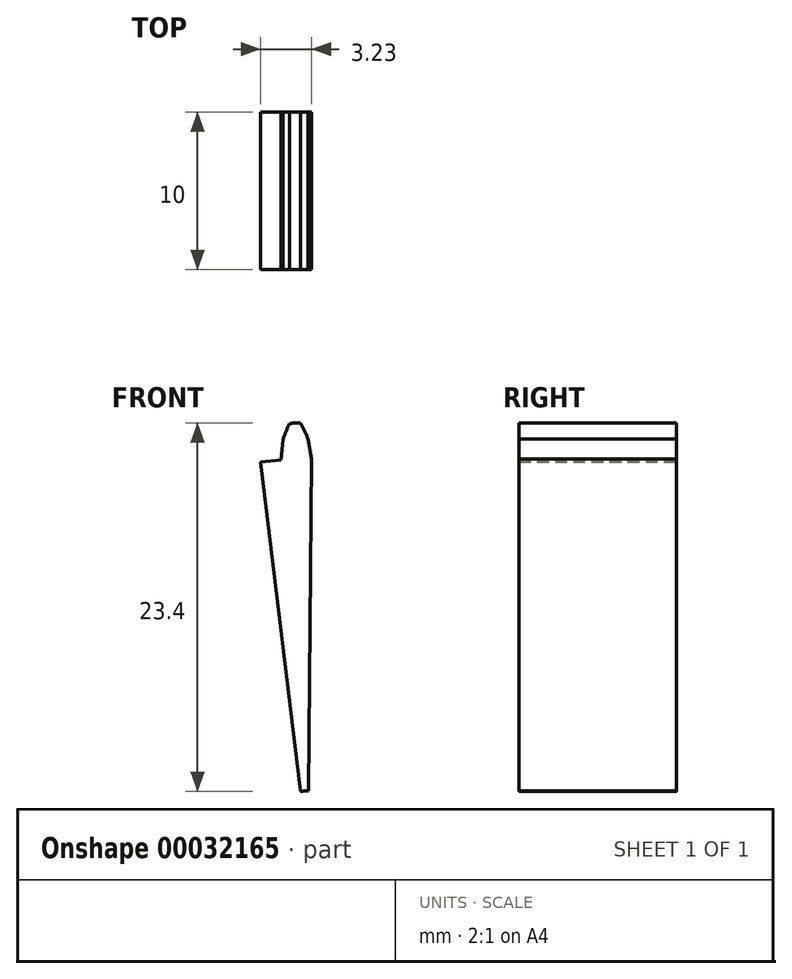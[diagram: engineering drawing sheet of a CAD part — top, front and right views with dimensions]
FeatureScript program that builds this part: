
annotation { "Feature Type Name" : "Feature", "Feature Type Description" : "" }
export const myFeature = defineFeature(function(context is Context, id is Id, definition is map)
    precondition{}
    {
        {
            var Q0;
            Q0=qCreatedBy(makeId("Front.planeOp"),FACE);
            var sketch = newSketch(context, id + "F0", { "sketchPlane" : qUnion([Q0])});
            skArc(sketch, "E0.trimOffspring", {"start": v(0, 26.31) * mm, "mid": v(-0.22, 26.83) * mm, "end": v(-0.48, 27.32) * mm});
            skArc(sketch, "E1.0.MirrorCS", {"start": v(-1.59, 26.26) * mm, "mid": v(-1.4, 26.8) * mm, "end": v(-1.17, 27.3) * mm});
            skArc(sketch, "E2.trimOffspring", {"start": v(-0.48, 27.32) * mm, "mid": v(-0.83, 27.31) * mm, "end": v(-1.17, 27.3) * mm});
            skCircle(sketch, "E3", {"center": v(0, -0.03) * mm, "radius": 29 * mm});
            skArc(sketch, "E4.trimOffspring", {"start": v(1.48, 24.98) * mm, "mid": v(0.85, 25.02) * mm, "end": v(0.21, 25.04) * mm});
            skLineSegment(sketch, "E5", {"start": v(-3.02, 24.86) * mm, "end": v(-1.72, 24.98) * mm});
            skCircle(sketch, "E6", {"center": v(0, 0) * mm, "radius": 3.95 * mm});
            skLineSegment(sketch, "E7", {"start": v(-3.5, 28.76) * mm, "end": v(0, 0) * mm});
            skLineSegment(sketch, "E8", {"start": v(-1.59, 26.26) * mm, "end": v(-1.72, 24.98) * mm});
            skLineSegment(sketch, "E9", {"start": v(0, 26.31) * mm, "end": v(0.21, 25.04) * mm});
            skLineSegment(sketch, "E10", {"start": v(0.24, 28.97) * mm, "end": v(0, 0) * mm});
            skSolve(sketch);
        }
        {
            var Q0;
            Q0=makeQuery(id+"FG2zr5kD53DtZhP_0.opExtrude","CAP_FACE",FACE,{"disambiguationData":[OSD([sQuery(id+"F0.wireOp",EDGE,"38f0ead0-3dfe-4054-9ca8-f6ac89a4f2fc"),sQuery(id+"F0.wireOp",EDGE,"E0.trimOffspring"),sQuery(id+"F0.wireOp",EDGE,"E1.0.MirrorCS"),sQuery(id+"F0.wireOp",EDGE,"ad14948e-b5b9-4d29-acd9-736fc249e560.0.MirrorCS"),sQuery(id+"F0.wireOp",EDGE,"E2.trimOffspring"),sQuery(id+"F0.wireOp",EDGE,"63f2db29-570f-450b-bac2-a88f50f61318.1.0"),sQuery(id+"F0.wireOp",EDGE,"63f2db29-570f-450b-bac2-a88f50f61318.1.1"),sQuery(id+"F0.wireOp",EDGE,"63f2db29-570f-450b-bac2-a88f50f61318.1.2"),sQuery(id+"F0.wireOp",EDGE,"63f2db29-570f-450b-bac2-a88f50f61318.1.3"),sQuery(id+"F0.wireOp",EDGE,"63f2db29-570f-450b-bac2-a88f50f61318.1.4"),sQuery(id+"F0.wireOp",EDGE,"63f2db29-570f-450b-bac2-a88f50f61318.2.0"),sQuery(id+"F0.wireOp",EDGE,"63f2db29-570f-450b-bac2-a88f50f61318.2.1"),sQuery(id+"F0.wireOp",EDGE,"63f2db29-570f-450b-bac2-a88f50f61318.2.2"),sQuery(id+"F0.wireOp",EDGE,"63f2db29-570f-450b-bac2-a88f50f61318.2.3"),sQuery(id+"F0.wireOp",EDGE,"63f2db29-570f-450b-bac2-a88f50f61318.2.4"),sQuery(id+"F0.wireOp",EDGE,"63f2db29-570f-450b-bac2-a88f50f61318.3.0"),sQuery(id+"F0.wireOp",EDGE,"63f2db29-570f-450b-bac2-a88f50f61318.3.1"),sQuery(id+"F0.wireOp",EDGE,"63f2db29-570f-450b-bac2-a88f50f61318.3.2"),sQuery(id+"F0.wireOp",EDGE,"63f2db29-570f-450b-bac2-a88f50f61318.3.3"),sQuery(id+"F0.wireOp",EDGE,"63f2db29-570f-450b-bac2-a88f50f61318.3.4"),sQuery(id+"F0.wireOp",EDGE,"63f2db29-570f-450b-bac2-a88f50f61318.4.0"),sQuery(id+"F0.wireOp",EDGE,"63f2db29-570f-450b-bac2-a88f50f61318.4.1"),sQuery(id+"F0.wireOp",EDGE,"63f2db29-570f-450b-bac2-a88f50f61318.4.2"),sQuery(id+"F0.wireOp",EDGE,"63f2db29-570f-450b-bac2-a88f50f61318.4.3"),sQuery(id+"F0.wireOp",EDGE,"63f2db29-570f-450b-bac2-a88f50f61318.4.4"),sQuery(id+"F0.wireOp",EDGE,"63f2db29-570f-450b-bac2-a88f50f61318.5.0"),sQuery(id+"F0.wireOp",EDGE,"63f2db29-570f-450b-bac2-a88f50f61318.5.1"),sQuery(id+"F0.wireOp",EDGE,"63f2db29-570f-450b-bac2-a88f50f61318.5.2"),sQuery(id+"F0.wireOp",EDGE,"63f2db29-570f-450b-bac2-a88f50f61318.5.3"),sQuery(id+"F0.wireOp",EDGE,"63f2db29-570f-450b-bac2-a88f50f61318.5.4"),sQuery(id+"F0.wireOp",EDGE,"63f2db29-570f-450b-bac2-a88f50f61318.6.0"),sQuery(id+"F0.wireOp",EDGE,"63f2db29-570f-450b-bac2-a88f50f61318.6.1"),sQuery(id+"F0.wireOp",EDGE,"63f2db29-570f-450b-bac2-a88f50f61318.6.2"),sQuery(id+"F0.wireOp",EDGE,"63f2db29-570f-450b-bac2-a88f50f61318.6.3"),sQuery(id+"F0.wireOp",EDGE,"63f2db29-570f-450b-bac2-a88f50f61318.6.4"),sQuery(id+"F0.wireOp",EDGE,"63f2db29-570f-450b-bac2-a88f50f61318.7.0"),sQuery(id+"F0.wireOp",EDGE,"63f2db29-570f-450b-bac2-a88f50f61318.7.1"),sQuery(id+"F0.wireOp",EDGE,"63f2db29-570f-450b-bac2-a88f50f61318.7.2"),sQuery(id+"F0.wireOp",EDGE,"63f2db29-570f-450b-bac2-a88f50f61318.7.3"),sQuery(id+"F0.wireOp",EDGE,"63f2db29-570f-450b-bac2-a88f50f61318.7.4"),sQuery(id+"F0.wireOp",EDGE,"63f2db29-570f-450b-bac2-a88f50f61318.8.0"),sQuery(id+"F0.wireOp",EDGE,"63f2db29-570f-450b-bac2-a88f50f61318.8.1"),sQuery(id+"F0.wireOp",EDGE,"63f2db29-570f-450b-bac2-a88f50f61318.8.2"),sQuery(id+"F0.wireOp",EDGE,"63f2db29-570f-450b-bac2-a88f50f61318.8.3"),sQuery(id+"F0.wireOp",EDGE,"63f2db29-570f-450b-bac2-a88f50f61318.8.4"),sQuery(id+"F0.wireOp",EDGE,"63f2db29-570f-450b-bac2-a88f50f61318.9.0"),sQuery(id+"F0.wireOp",EDGE,"63f2db29-570f-450b-bac2-a88f50f61318.9.1"),sQuery(id+"F0.wireOp",EDGE,"63f2db29-570f-450b-bac2-a88f50f61318.9.2"),sQuery(id+"F0.wireOp",EDGE,"63f2db29-570f-450b-bac2-a88f50f61318.9.3"),sQuery(id+"F0.wireOp",EDGE,"63f2db29-570f-450b-bac2-a88f50f61318.9.4"),sQuery(id+"F0.wireOp",EDGE,"63f2db29-570f-450b-bac2-a88f50f61318.10.0"),sQuery(id+"F0.wireOp",EDGE,"63f2db29-570f-450b-bac2-a88f50f61318.10.1"),sQuery(id+"F0.wireOp",EDGE,"63f2db29-570f-450b-bac2-a88f50f61318.10.2"),sQuery(id+"F0.wireOp",EDGE,"63f2db29-570f-450b-bac2-a88f50f61318.10.3"),sQuery(id+"F0.wireOp",EDGE,"63f2db29-570f-450b-bac2-a88f50f61318.10.4"),sQuery(id+"F0.wireOp",EDGE,"63f2db29-570f-450b-bac2-a88f50f61318.11.0"),sQuery(id+"F0.wireOp",EDGE,"63f2db29-570f-450b-bac2-a88f50f61318.11.1"),sQuery(id+"F0.wireOp",EDGE,"63f2db29-570f-450b-bac2-a88f50f61318.11.2"),sQuery(id+"F0.wireOp",EDGE,"63f2db29-570f-450b-bac2-a88f50f61318.11.3"),sQuery(id+"F0.wireOp",EDGE,"63f2db29-570f-450b-bac2-a88f50f61318.11.4"),sQuery(id+"F0.wireOp",EDGE,"63f2db29-570f-450b-bac2-a88f50f61318.12.0"),sQuery(id+"F0.wireOp",EDGE,"63f2db29-570f-450b-bac2-a88f50f61318.12.1"),sQuery(id+"F0.wireOp",EDGE,"63f2db29-570f-450b-bac2-a88f50f61318.12.2"),sQuery(id+"F0.wireOp",EDGE,"63f2db29-570f-450b-bac2-a88f50f61318.12.3"),sQuery(id+"F0.wireOp",EDGE,"63f2db29-570f-450b-bac2-a88f50f61318.12.4"),sQuery(id+"F0.wireOp",EDGE,"63f2db29-570f-450b-bac2-a88f50f61318.13.0"),sQuery(id+"F0.wireOp",EDGE,"63f2db29-570f-450b-bac2-a88f50f61318.13.1"),sQuery(id+"F0.wireOp",EDGE,"63f2db29-570f-450b-bac2-a88f50f61318.13.2"),sQuery(id+"F0.wireOp",EDGE,"63f2db29-570f-450b-bac2-a88f50f61318.13.3"),sQuery(id+"F0.wireOp",EDGE,"63f2db29-570f-450b-bac2-a88f50f61318.13.4"),sQuery(id+"F0.wireOp",EDGE,"63f2db29-570f-450b-bac2-a88f50f61318.14.0"),sQuery(id+"F0.wireOp",EDGE,"63f2db29-570f-450b-bac2-a88f50f61318.14.1"),sQuery(id+"F0.wireOp",EDGE,"63f2db29-570f-450b-bac2-a88f50f61318.14.2"),sQuery(id+"F0.wireOp",EDGE,"63f2db29-570f-450b-bac2-a88f50f61318.14.3"),sQuery(id+"F0.wireOp",EDGE,"63f2db29-570f-450b-bac2-a88f50f61318.14.4"),sQuery(id+"F0.wireOp",EDGE,"63f2db29-570f-450b-bac2-a88f50f61318.15.0"),sQuery(id+"F0.wireOp",EDGE,"63f2db29-570f-450b-bac2-a88f50f61318.15.1"),sQuery(id+"F0.wireOp",EDGE,"63f2db29-570f-450b-bac2-a88f50f61318.15.2"),sQuery(id+"F0.wireOp",EDGE,"63f2db29-570f-450b-bac2-a88f50f61318.15.3"),sQuery(id+"F0.wireOp",EDGE,"63f2db29-570f-450b-bac2-a88f50f61318.15.4"),sQuery(id+"F0.wireOp",EDGE,"63f2db29-570f-450b-bac2-a88f50f61318.16.0"),sQuery(id+"F0.wireOp",EDGE,"63f2db29-570f-450b-bac2-a88f50f61318.16.1"),sQuery(id+"F0.wireOp",EDGE,"63f2db29-570f-450b-bac2-a88f50f61318.16.2"),sQuery(id+"F0.wireOp",EDGE,"63f2db29-570f-450b-bac2-a88f50f61318.16.3"),sQuery(id+"F0.wireOp",EDGE,"63f2db29-570f-450b-bac2-a88f50f61318.16.4"),sQuery(id+"F0.wireOp",EDGE,"63f2db29-570f-450b-bac2-a88f50f61318.17.0"),sQuery(id+"F0.wireOp",EDGE,"63f2db29-570f-450b-bac2-a88f50f61318.17.1"),sQuery(id+"F0.wireOp",EDGE,"63f2db29-570f-450b-bac2-a88f50f61318.17.2"),sQuery(id+"F0.wireOp",EDGE,"63f2db29-570f-450b-bac2-a88f50f61318.17.3"),sQuery(id+"F0.wireOp",EDGE,"63f2db29-570f-450b-bac2-a88f50f61318.17.4"),sQuery(id+"F0.wireOp",EDGE,"63f2db29-570f-450b-bac2-a88f50f61318.18.0"),sQuery(id+"F0.wireOp",EDGE,"63f2db29-570f-450b-bac2-a88f50f61318.18.1"),sQuery(id+"F0.wireOp",EDGE,"63f2db29-570f-450b-bac2-a88f50f61318.18.2"),sQuery(id+"F0.wireOp",EDGE,"63f2db29-570f-450b-bac2-a88f50f61318.18.3"),sQuery(id+"F0.wireOp",EDGE,"63f2db29-570f-450b-bac2-a88f50f61318.18.4"),sQuery(id+"F0.wireOp",EDGE,"63f2db29-570f-450b-bac2-a88f50f61318.19.0"),sQuery(id+"F0.wireOp",EDGE,"63f2db29-570f-450b-bac2-a88f50f61318.19.1"),sQuery(id+"F0.wireOp",EDGE,"63f2db29-570f-450b-bac2-a88f50f61318.19.2"),sQuery(id+"F0.wireOp",EDGE,"63f2db29-570f-450b-bac2-a88f50f61318.19.3"),sQuery(id+"F0.wireOp",EDGE,"63f2db29-570f-450b-bac2-a88f50f61318.19.4"),sQuery(id+"F0.wireOp",EDGE,"63f2db29-570f-450b-bac2-a88f50f61318.20.0"),sQuery(id+"F0.wireOp",EDGE,"63f2db29-570f-450b-bac2-a88f50f61318.20.1"),sQuery(id+"F0.wireOp",EDGE,"63f2db29-570f-450b-bac2-a88f50f61318.20.2"),sQuery(id+"F0.wireOp",EDGE,"63f2db29-570f-450b-bac2-a88f50f61318.20.3"),sQuery(id+"F0.wireOp",EDGE,"63f2db29-570f-450b-bac2-a88f50f61318.20.4"),sQuery(id+"F0.wireOp",EDGE,"63f2db29-570f-450b-bac2-a88f50f61318.21.0"),sQuery(id+"F0.wireOp",EDGE,"63f2db29-570f-450b-bac2-a88f50f61318.21.1"),sQuery(id+"F0.wireOp",EDGE,"63f2db29-570f-450b-bac2-a88f50f61318.21.2"),sQuery(id+"F0.wireOp",EDGE,"63f2db29-570f-450b-bac2-a88f50f61318.21.3"),sQuery(id+"F0.wireOp",EDGE,"63f2db29-570f-450b-bac2-a88f50f61318.21.4"),sQuery(id+"F0.wireOp",EDGE,"63f2db29-570f-450b-bac2-a88f50f61318.22.0"),sQuery(id+"F0.wireOp",EDGE,"63f2db29-570f-450b-bac2-a88f50f61318.22.1"),sQuery(id+"F0.wireOp",EDGE,"63f2db29-570f-450b-bac2-a88f50f61318.22.2"),sQuery(id+"F0.wireOp",EDGE,"63f2db29-570f-450b-bac2-a88f50f61318.22.3"),sQuery(id+"F0.wireOp",EDGE,"63f2db29-570f-450b-bac2-a88f50f61318.22.4"),sQuery(id+"F0.wireOp",EDGE,"63f2db29-570f-450b-bac2-a88f50f61318.23.0"),sQuery(id+"F0.wireOp",EDGE,"63f2db29-570f-450b-bac2-a88f50f61318.23.1"),sQuery(id+"F0.wireOp",EDGE,"63f2db29-570f-450b-bac2-a88f50f61318.23.2"),sQuery(id+"F0.wireOp",EDGE,"63f2db29-570f-450b-bac2-a88f50f61318.23.3"),sQuery(id+"F0.wireOp",EDGE,"63f2db29-570f-450b-bac2-a88f50f61318.23.4"),sQuery(id+"F0.wireOp",EDGE,"63f2db29-570f-450b-bac2-a88f50f61318.24.0"),sQuery(id+"F0.wireOp",EDGE,"63f2db29-570f-450b-bac2-a88f50f61318.24.1"),sQuery(id+"F0.wireOp",EDGE,"63f2db29-570f-450b-bac2-a88f50f61318.24.2"),sQuery(id+"F0.wireOp",EDGE,"63f2db29-570f-450b-bac2-a88f50f61318.24.3"),sQuery(id+"F0.wireOp",EDGE,"63f2db29-570f-450b-bac2-a88f50f61318.24.4"),sQuery(id+"F0.wireOp",EDGE,"63f2db29-570f-450b-bac2-a88f50f61318.25.0"),sQuery(id+"F0.wireOp",EDGE,"63f2db29-570f-450b-bac2-a88f50f61318.25.1"),sQuery(id+"F0.wireOp",EDGE,"63f2db29-570f-450b-bac2-a88f50f61318.25.2"),sQuery(id+"F0.wireOp",EDGE,"63f2db29-570f-450b-bac2-a88f50f61318.25.3"),sQuery(id+"F0.wireOp",EDGE,"63f2db29-570f-450b-bac2-a88f50f61318.25.4"),sQuery(id+"F0.wireOp",EDGE,"63f2db29-570f-450b-bac2-a88f50f61318.26.0"),sQuery(id+"F0.wireOp",EDGE,"63f2db29-570f-450b-bac2-a88f50f61318.26.1"),sQuery(id+"F0.wireOp",EDGE,"63f2db29-570f-450b-bac2-a88f50f61318.26.2"),sQuery(id+"F0.wireOp",EDGE,"63f2db29-570f-450b-bac2-a88f50f61318.26.3"),sQuery(id+"F0.wireOp",EDGE,"63f2db29-570f-450b-bac2-a88f50f61318.26.4"),sQuery(id+"F0.wireOp",EDGE,"63f2db29-570f-450b-bac2-a88f50f61318.27.0"),sQuery(id+"F0.wireOp",EDGE,"63f2db29-570f-450b-bac2-a88f50f61318.27.1"),sQuery(id+"F0.wireOp",EDGE,"63f2db29-570f-450b-bac2-a88f50f61318.27.2"),sQuery(id+"F0.wireOp",EDGE,"63f2db29-570f-450b-bac2-a88f50f61318.27.3"),sQuery(id+"F0.wireOp",EDGE,"63f2db29-570f-450b-bac2-a88f50f61318.27.4"),sQuery(id+"F0.wireOp",EDGE,"63f2db29-570f-450b-bac2-a88f50f61318.28.0"),sQuery(id+"F0.wireOp",EDGE,"63f2db29-570f-450b-bac2-a88f50f61318.28.1"),sQuery(id+"F0.wireOp",EDGE,"63f2db29-570f-450b-bac2-a88f50f61318.28.2"),sQuery(id+"F0.wireOp",EDGE,"63f2db29-570f-450b-bac2-a88f50f61318.28.3"),sQuery(id+"F0.wireOp",EDGE,"63f2db29-570f-450b-bac2-a88f50f61318.28.4"),sQuery(id+"F0.wireOp",EDGE,"63f2db29-570f-450b-bac2-a88f50f61318.29.0"),sQuery(id+"F0.wireOp",EDGE,"63f2db29-570f-450b-bac2-a88f50f61318.29.1"),sQuery(id+"F0.wireOp",EDGE,"63f2db29-570f-450b-bac2-a88f50f61318.29.2"),sQuery(id+"F0.wireOp",EDGE,"63f2db29-570f-450b-bac2-a88f50f61318.29.3"),sQuery(id+"F0.wireOp",EDGE,"63f2db29-570f-450b-bac2-a88f50f61318.29.4"),sQuery(id+"F0.wireOp",EDGE,"63f2db29-570f-450b-bac2-a88f50f61318.30.0"),sQuery(id+"F0.wireOp",EDGE,"63f2db29-570f-450b-bac2-a88f50f61318.30.1"),sQuery(id+"F0.wireOp",EDGE,"63f2db29-570f-450b-bac2-a88f50f61318.30.2"),sQuery(id+"F0.wireOp",EDGE,"63f2db29-570f-450b-bac2-a88f50f61318.30.3"),sQuery(id+"F0.wireOp",EDGE,"63f2db29-570f-450b-bac2-a88f50f61318.30.4"),sQuery(id+"F0.wireOp",EDGE,"63f2db29-570f-450b-bac2-a88f50f61318.31.0"),sQuery(id+"F0.wireOp",EDGE,"63f2db29-570f-450b-bac2-a88f50f61318.31.1"),sQuery(id+"F0.wireOp",EDGE,"63f2db29-570f-450b-bac2-a88f50f61318.31.2"),sQuery(id+"F0.wireOp",EDGE,"63f2db29-570f-450b-bac2-a88f50f61318.31.3"),sQuery(id+"F0.wireOp",EDGE,"63f2db29-570f-450b-bac2-a88f50f61318.31.4"),sQuery(id+"F0.wireOp",EDGE,"63f2db29-570f-450b-bac2-a88f50f61318.32.0"),sQuery(id+"F0.wireOp",EDGE,"63f2db29-570f-450b-bac2-a88f50f61318.32.1"),sQuery(id+"F0.wireOp",EDGE,"63f2db29-570f-450b-bac2-a88f50f61318.32.2"),sQuery(id+"F0.wireOp",EDGE,"63f2db29-570f-450b-bac2-a88f50f61318.32.3"),sQuery(id+"F0.wireOp",EDGE,"63f2db29-570f-450b-bac2-a88f50f61318.32.4"),sQuery(id+"F0.wireOp",EDGE,"63f2db29-570f-450b-bac2-a88f50f61318.33.0"),sQuery(id+"F0.wireOp",EDGE,"63f2db29-570f-450b-bac2-a88f50f61318.33.1"),sQuery(id+"F0.wireOp",EDGE,"63f2db29-570f-450b-bac2-a88f50f61318.33.2"),sQuery(id+"F0.wireOp",EDGE,"63f2db29-570f-450b-bac2-a88f50f61318.33.3"),sQuery(id+"F0.wireOp",EDGE,"63f2db29-570f-450b-bac2-a88f50f61318.33.4"),sQuery(id+"F0.wireOp",EDGE,"63f2db29-570f-450b-bac2-a88f50f61318.34.0"),sQuery(id+"F0.wireOp",EDGE,"63f2db29-570f-450b-bac2-a88f50f61318.34.1"),sQuery(id+"F0.wireOp",EDGE,"63f2db29-570f-450b-bac2-a88f50f61318.34.2"),sQuery(id+"F0.wireOp",EDGE,"63f2db29-570f-450b-bac2-a88f50f61318.34.3"),sQuery(id+"F0.wireOp",EDGE,"63f2db29-570f-450b-bac2-a88f50f61318.34.4"),sQuery(id+"F0.wireOp",EDGE,"63f2db29-570f-450b-bac2-a88f50f61318.35.0"),sQuery(id+"F0.wireOp",EDGE,"63f2db29-570f-450b-bac2-a88f50f61318.35.1"),sQuery(id+"F0.wireOp",EDGE,"63f2db29-570f-450b-bac2-a88f50f61318.35.2"),sQuery(id+"F0.wireOp",EDGE,"63f2db29-570f-450b-bac2-a88f50f61318.35.3"),sQuery(id+"F0.wireOp",EDGE,"63f2db29-570f-450b-bac2-a88f50f61318.35.4"),sQuery(id+"F0.wireOp",EDGE,"63f2db29-570f-450b-bac2-a88f50f61318.36.0"),sQuery(id+"F0.wireOp",EDGE,"63f2db29-570f-450b-bac2-a88f50f61318.36.1"),sQuery(id+"F0.wireOp",EDGE,"63f2db29-570f-450b-bac2-a88f50f61318.36.2"),sQuery(id+"F0.wireOp",EDGE,"63f2db29-570f-450b-bac2-a88f50f61318.36.3"),sQuery(id+"F0.wireOp",EDGE,"63f2db29-570f-450b-bac2-a88f50f61318.36.4"),sQuery(id+"F0.wireOp",EDGE,"63f2db29-570f-450b-bac2-a88f50f61318.37.0"),sQuery(id+"F0.wireOp",EDGE,"63f2db29-570f-450b-bac2-a88f50f61318.37.1"),sQuery(id+"F0.wireOp",EDGE,"63f2db29-570f-450b-bac2-a88f50f61318.37.2"),sQuery(id+"F0.wireOp",EDGE,"63f2db29-570f-450b-bac2-a88f50f61318.37.3"),sQuery(id+"F0.wireOp",EDGE,"63f2db29-570f-450b-bac2-a88f50f61318.37.4"),sQuery(id+"F0.wireOp",EDGE,"63f2db29-570f-450b-bac2-a88f50f61318.38.0"),sQuery(id+"F0.wireOp",EDGE,"63f2db29-570f-450b-bac2-a88f50f61318.38.1"),sQuery(id+"F0.wireOp",EDGE,"63f2db29-570f-450b-bac2-a88f50f61318.38.2"),sQuery(id+"F0.wireOp",EDGE,"63f2db29-570f-450b-bac2-a88f50f61318.38.3"),sQuery(id+"F0.wireOp",EDGE,"63f2db29-570f-450b-bac2-a88f50f61318.38.4"),sQuery(id+"F0.wireOp",EDGE,"63f2db29-570f-450b-bac2-a88f50f61318.39.0"),sQuery(id+"F0.wireOp",EDGE,"63f2db29-570f-450b-bac2-a88f50f61318.39.1"),sQuery(id+"F0.wireOp",EDGE,"63f2db29-570f-450b-bac2-a88f50f61318.39.2"),sQuery(id+"F0.wireOp",EDGE,"63f2db29-570f-450b-bac2-a88f50f61318.39.3"),sQuery(id+"F0.wireOp",EDGE,"63f2db29-570f-450b-bac2-a88f50f61318.39.4"),sQuery(id+"F0.wireOp",EDGE,"63f2db29-570f-450b-bac2-a88f50f61318.40.0"),sQuery(id+"F0.wireOp",EDGE,"63f2db29-570f-450b-bac2-a88f50f61318.40.1"),sQuery(id+"F0.wireOp",EDGE,"63f2db29-570f-450b-bac2-a88f50f61318.40.2"),sQuery(id+"F0.wireOp",EDGE,"63f2db29-570f-450b-bac2-a88f50f61318.40.3"),sQuery(id+"F0.wireOp",EDGE,"63f2db29-570f-450b-bac2-a88f50f61318.40.4"),sQuery(id+"F0.wireOp",EDGE,"63f2db29-570f-450b-bac2-a88f50f61318.41.0"),sQuery(id+"F0.wireOp",EDGE,"63f2db29-570f-450b-bac2-a88f50f61318.41.1"),sQuery(id+"F0.wireOp",EDGE,"63f2db29-570f-450b-bac2-a88f50f61318.41.2"),sQuery(id+"F0.wireOp",EDGE,"63f2db29-570f-450b-bac2-a88f50f61318.41.3"),sQuery(id+"F0.wireOp",EDGE,"63f2db29-570f-450b-bac2-a88f50f61318.41.4"),sQuery(id+"F0.wireOp",EDGE,"63f2db29-570f-450b-bac2-a88f50f61318.42.0"),sQuery(id+"F0.wireOp",EDGE,"63f2db29-570f-450b-bac2-a88f50f61318.42.1"),sQuery(id+"F0.wireOp",EDGE,"63f2db29-570f-450b-bac2-a88f50f61318.42.2"),sQuery(id+"F0.wireOp",EDGE,"63f2db29-570f-450b-bac2-a88f50f61318.42.3"),sQuery(id+"F0.wireOp",EDGE,"63f2db29-570f-450b-bac2-a88f50f61318.42.4"),sQuery(id+"F0.wireOp",EDGE,"63f2db29-570f-450b-bac2-a88f50f61318.43.0"),sQuery(id+"F0.wireOp",EDGE,"63f2db29-570f-450b-bac2-a88f50f61318.43.1"),sQuery(id+"F0.wireOp",EDGE,"63f2db29-570f-450b-bac2-a88f50f61318.43.2"),sQuery(id+"F0.wireOp",EDGE,"63f2db29-570f-450b-bac2-a88f50f61318.43.3"),sQuery(id+"F0.wireOp",EDGE,"63f2db29-570f-450b-bac2-a88f50f61318.43.4"),sQuery(id+"F0.wireOp",EDGE,"63f2db29-570f-450b-bac2-a88f50f61318.44.0"),sQuery(id+"F0.wireOp",EDGE,"63f2db29-570f-450b-bac2-a88f50f61318.44.1"),sQuery(id+"F0.wireOp",EDGE,"63f2db29-570f-450b-bac2-a88f50f61318.44.2"),sQuery(id+"F0.wireOp",EDGE,"63f2db29-570f-450b-bac2-a88f50f61318.44.3"),sQuery(id+"F0.wireOp",EDGE,"63f2db29-570f-450b-bac2-a88f50f61318.44.4"),sQuery(id+"F0.wireOp",EDGE,"63f2db29-570f-450b-bac2-a88f50f61318.45.0"),sQuery(id+"F0.wireOp",EDGE,"63f2db29-570f-450b-bac2-a88f50f61318.45.1"),sQuery(id+"F0.wireOp",EDGE,"63f2db29-570f-450b-bac2-a88f50f61318.45.2"),sQuery(id+"F0.wireOp",EDGE,"63f2db29-570f-450b-bac2-a88f50f61318.45.3"),sQuery(id+"F0.wireOp",EDGE,"63f2db29-570f-450b-bac2-a88f50f61318.45.4"),sQuery(id+"F0.wireOp",EDGE,"63f2db29-570f-450b-bac2-a88f50f61318.46.0"),sQuery(id+"F0.wireOp",EDGE,"63f2db29-570f-450b-bac2-a88f50f61318.46.1"),sQuery(id+"F0.wireOp",EDGE,"63f2db29-570f-450b-bac2-a88f50f61318.46.2"),sQuery(id+"F0.wireOp",EDGE,"63f2db29-570f-450b-bac2-a88f50f61318.46.3"),sQuery(id+"F0.wireOp",EDGE,"63f2db29-570f-450b-bac2-a88f50f61318.46.4"),sQuery(id+"F0.wireOp",EDGE,"63f2db29-570f-450b-bac2-a88f50f61318.47.0"),sQuery(id+"F0.wireOp",EDGE,"63f2db29-570f-450b-bac2-a88f50f61318.47.1"),sQuery(id+"F0.wireOp",EDGE,"63f2db29-570f-450b-bac2-a88f50f61318.47.2"),sQuery(id+"F0.wireOp",EDGE,"63f2db29-570f-450b-bac2-a88f50f61318.47.3"),sQuery(id+"F0.wireOp",EDGE,"63f2db29-570f-450b-bac2-a88f50f61318.47.4"),sQuery(id+"F0.wireOp",EDGE,"63f2db29-570f-450b-bac2-a88f50f61318.48.0"),sQuery(id+"F0.wireOp",EDGE,"63f2db29-570f-450b-bac2-a88f50f61318.48.1"),sQuery(id+"F0.wireOp",EDGE,"63f2db29-570f-450b-bac2-a88f50f61318.48.2"),sQuery(id+"F0.wireOp",EDGE,"63f2db29-570f-450b-bac2-a88f50f61318.48.3"),sQuery(id+"F0.wireOp",EDGE,"63f2db29-570f-450b-bac2-a88f50f61318.48.4"),sQuery(id+"F0.wireOp",EDGE,"63f2db29-570f-450b-bac2-a88f50f61318.49.0"),sQuery(id+"F0.wireOp",EDGE,"63f2db29-570f-450b-bac2-a88f50f61318.49.1"),sQuery(id+"F0.wireOp",EDGE,"63f2db29-570f-450b-bac2-a88f50f61318.49.2"),sQuery(id+"F0.wireOp",EDGE,"63f2db29-570f-450b-bac2-a88f50f61318.49.3"),sQuery(id+"F0.wireOp",EDGE,"63f2db29-570f-450b-bac2-a88f50f61318.49.4"),sQuery(id+"F0.wireOp",EDGE,"63f2db29-570f-450b-bac2-a88f50f61318.50.0"),sQuery(id+"F0.wireOp",EDGE,"63f2db29-570f-450b-bac2-a88f50f61318.50.1"),sQuery(id+"F0.wireOp",EDGE,"63f2db29-570f-450b-bac2-a88f50f61318.50.2"),sQuery(id+"F0.wireOp",EDGE,"63f2db29-570f-450b-bac2-a88f50f61318.50.3"),sQuery(id+"F0.wireOp",EDGE,"63f2db29-570f-450b-bac2-a88f50f61318.50.4"),sQuery(id+"F0.wireOp",EDGE,"63f2db29-570f-450b-bac2-a88f50f61318.51.0"),sQuery(id+"F0.wireOp",EDGE,"63f2db29-570f-450b-bac2-a88f50f61318.51.1"),sQuery(id+"F0.wireOp",EDGE,"63f2db29-570f-450b-bac2-a88f50f61318.51.2"),sQuery(id+"F0.wireOp",EDGE,"63f2db29-570f-450b-bac2-a88f50f61318.51.3"),sQuery(id+"F0.wireOp",EDGE,"63f2db29-570f-450b-bac2-a88f50f61318.51.4"),sQuery(id+"F0.wireOp",EDGE,"E3"),sQuery(id+"F0.wireOp",EDGE,"E4.trimOffspring"),sQuery(id+"F0.wireOp",EDGE,"7a9f3865-c45e-4aec-9efc-5f652d7d6185.trimOffspring"),sQuery(id+"F0.wireOp",EDGE,"5faada67-5688-4a5a-b827-7b7abcb62621.trimOffspring"),sQuery(id+"F0.wireOp",EDGE,"abeeb76f-2569-496c-af8d-d22e55683bed.trimOffspring"),sQuery(id+"F0.wireOp",EDGE,"867d8221-c4fc-4f4b-a222-91b8296d2518.trimOffspring"),sQuery(id+"F0.wireOp",EDGE,"2813aa4e-2c4a-4562-a643-02c9683fda06.trimOffspring"),sQuery(id+"F0.wireOp",EDGE,"c04c359a-9abc-41c0-8ab9-bbb745a42cc9.trimOffspring"),sQuery(id+"F0.wireOp",EDGE,"c8408685-7f1a-498a-aeef-9e7f63cb7536.trimOffspring"),sQuery(id+"F0.wireOp",EDGE,"eb91e5f3-f527-4988-984d-6cdc1fdbe117.trimOffspring"),sQuery(id+"F0.wireOp",EDGE,"612ca8e1-1b05-4d7f-abe8-2e8448acf232.trimOffspring"),sQuery(id+"F0.wireOp",EDGE,"9a973068-169f-4eaf-93d9-6f1640aa539e.trimOffspring"),sQuery(id+"F0.wireOp",EDGE,"50f89e6b-dcc1-46c4-9f7e-b7e3d11b6dd9.trimOffspring"),sQuery(id+"F0.wireOp",EDGE,"b03b4f95-36eb-4f80-8184-76a8b445329b.trimOffspring"),sQuery(id+"F0.wireOp",EDGE,"3a98c58a-bf96-4c12-b085-26acecc9e4e1"),sQuery(id+"F0.wireOp",EDGE,"E5"),sQuery(id+"F0.wireOp",EDGE,"2c6da735-7088-4754-8413-59bc0f926720.trimOffspring"),sQuery(id+"F0.wireOp",EDGE,"ade7b5b6-737c-4785-9f76-ef35d28e0981.trimOffspring"),sQuery(id+"F0.wireOp",EDGE,"2c0f415a-7010-4b7a-bb9e-fc4b0881021c.trimOffspring"),sQuery(id+"F0.wireOp",EDGE,"0d5fd491-d67e-48a2-bdfa-9a4c3583840a.trimOffspring"),sQuery(id+"F0.wireOp",EDGE,"8cdd9e30-2819-40d8-bb54-b678b37e6bf5.trimOffspring"),sQuery(id+"F0.wireOp",EDGE,"88ea0e39-c363-4707-9812-97d5ff174c56.trimOffspring"),sQuery(id+"F0.wireOp",EDGE,"989946fd-1037-4bd6-89dc-2b6c5901de2a.trimOffspring"),sQuery(id+"F0.wireOp",EDGE,"3ce143e8-0107-41c3-819a-47e98e7ed5bc.trimOffspring"),sQuery(id+"F0.wireOp",EDGE,"c8afc288-4af5-4589-87c1-3547a6f938d0.trimOffspring"),sQuery(id+"F0.wireOp",EDGE,"c138ff95-b059-4b4a-8455-97e1cad64c83.trimOffspring"),sQuery(id+"F0.wireOp",EDGE,"ea1d337a-8259-4ee1-aade-fa127246008a.trimOffspring"),sQuery(id+"F0.wireOp",EDGE,"44d0170c-7aaf-4ea9-9bd7-26fe7855f7d0.trimOffspring"),sQuery(id+"F0.wireOp",EDGE,"55913379-09a8-4eb4-ae11-4ded71899b5e.trimOffspring"),sQuery(id+"F0.wireOp",EDGE,"31e856b4-fd0f-4e47-b5c2-4b0938dd5c89.trimOffspring"),sQuery(id+"F0.wireOp",EDGE,"0592b6a2-bfcf-40c7-b849-7d3d9d1f5655.trimOffspring"),sQuery(id+"F0.wireOp",EDGE,"e7497034-62f9-4229-b1bf-218c8b6f6a86.trimOffspring"),sQuery(id+"F0.wireOp",EDGE,"dc04b24d-ae36-4f84-85ff-7db030768312.trimOffspring"),sQuery(id+"F0.wireOp",EDGE,"615b480f-cffa-4957-b98f-862f888a044f.trimOffspring"),sQuery(id+"F0.wireOp",EDGE,"6f331aaf-05b2-4322-9272-68b8997a4325.trimOffspring"),sQuery(id+"F0.wireOp",EDGE,"d688b532-cdf5-4a01-8041-3558e50b6398.trimOffspring"),sQuery(id+"F0.wireOp",EDGE,"9e8fa21a-4532-4236-b037-0fe7c4738b8b.trimOffspring"),sQuery(id+"F0.wireOp",EDGE,"a08334cc-682b-4518-8a9e-90b9941ce23d.trimOffspring"),sQuery(id+"F0.wireOp",EDGE,"05e357b3-4102-42e9-87e2-9740b91f9d15.trimOffspring"),sQuery(id+"F0.wireOp",EDGE,"e833ced3-cb41-4280-b25e-ca7b53ac7992.trimOffspring"),sQuery(id+"F0.wireOp",EDGE,"9c1b2f2c-1c1c-47ee-af06-fd2841a4cafb.trimOffspring"),sQuery(id+"F0.wireOp",EDGE,"7db17ab2-7f59-42c4-b6db-f0475d58b537.trimOffspring"),sQuery(id+"F0.wireOp",EDGE,"9e5a76b1-f482-4253-a09f-498daebb1eca.trimOffspring"),sQuery(id+"F0.wireOp",EDGE,"fa09d571-d582-4ed0-8fc1-8744c921fc20.trimOffspring"),sQuery(id+"F0.wireOp",EDGE,"d5158141-809e-4ad2-bb5f-c91a4cdd387c.trimOffspring"),sQuery(id+"F0.wireOp",EDGE,"8edda4ff-5989-44e9-816a-461125b27849.trimOffspring"),sQuery(id+"F0.wireOp",EDGE,"642530d4-5282-4eca-aeba-3414806f050f.trimOffspring"),sQuery(id+"F0.wireOp",EDGE,"b82faa7a-d36c-4912-83a4-f790ae33aee0.trimOffspring"),sQuery(id+"F0.wireOp",EDGE,"5538aa7d-4870-4a3f-9df8-725cb2b55773"),sQuery(id+"F0.wireOp",EDGE,"a3723c29-ed7d-4e54-ade2-591849b537ff"),sQuery(id+"F0.wireOp",EDGE,"803ba892-a676-43cd-97c6-2f3b72d865be"),sQuery(id+"F0.wireOp",EDGE,"9613aab8-4a67-4989-851e-07c056218bb2"),sQuery(id+"F0.wireOp",EDGE,"05e026aa-e1d3-4a9c-999a-7ee55c6a69fe")])],"isStart":true});
            var sketch = newSketch(context, id + "F1", { "sketchPlane" : qUnion([Q0])});
            skCircle(sketch, "E11.0", {"center": v(0, -0.03) * mm, "radius": 29 * mm});
            skSolve(sketch);
        }
        {
            var Q0;
            Q0=makeQuery(id+"F0.imprint","IMPRINT",FACE,{"disambiguationData":[TD([[makeQuery(id+"F0.imprint","IMPRINT",EDGE,{"derivedFrom":sQuery(id+"F0.wireOp",EDGE,"E0.trimOffspring")}),1.0]])]});
            extrude(context, id + "F2", {"entities" : qUnion([Q0]), "depth" : 10 * mm});
        }
        {
            var Q0;
            Q0=makeQuery(id+"F2.opExtrude","SWEPT_BODY",BODY,{"disambiguationData":[OSD([sQuery(id+"F0.wireOp",EDGE,"E0.trimOffspring"),sQuery(id+"F0.wireOp",EDGE,"E1.0.MirrorCS"),sQuery(id+"F0.wireOp",EDGE,"E2.trimOffspring"),sQuery(id+"F0.wireOp",EDGE,"E5"),sQuery(id+"F0.wireOp",EDGE,"E6"),sQuery(id+"F0.wireOp",EDGE,"E7"),sQuery(id+"F0.wireOp",EDGE,"E8"),sQuery(id+"F0.wireOp",EDGE,"E9"),sQuery(id+"F0.wireOp",EDGE,"E10")])]});
            transform(context, id + "F3", {"entities" : qUnion([Q0]), "transformType" : TransformType.TRANSLATION_3D, "dx" : 0 * mm, "dy" : 0 * mm, "dz" : .5 * mm, "makeCopy" : false});
        }
    });
